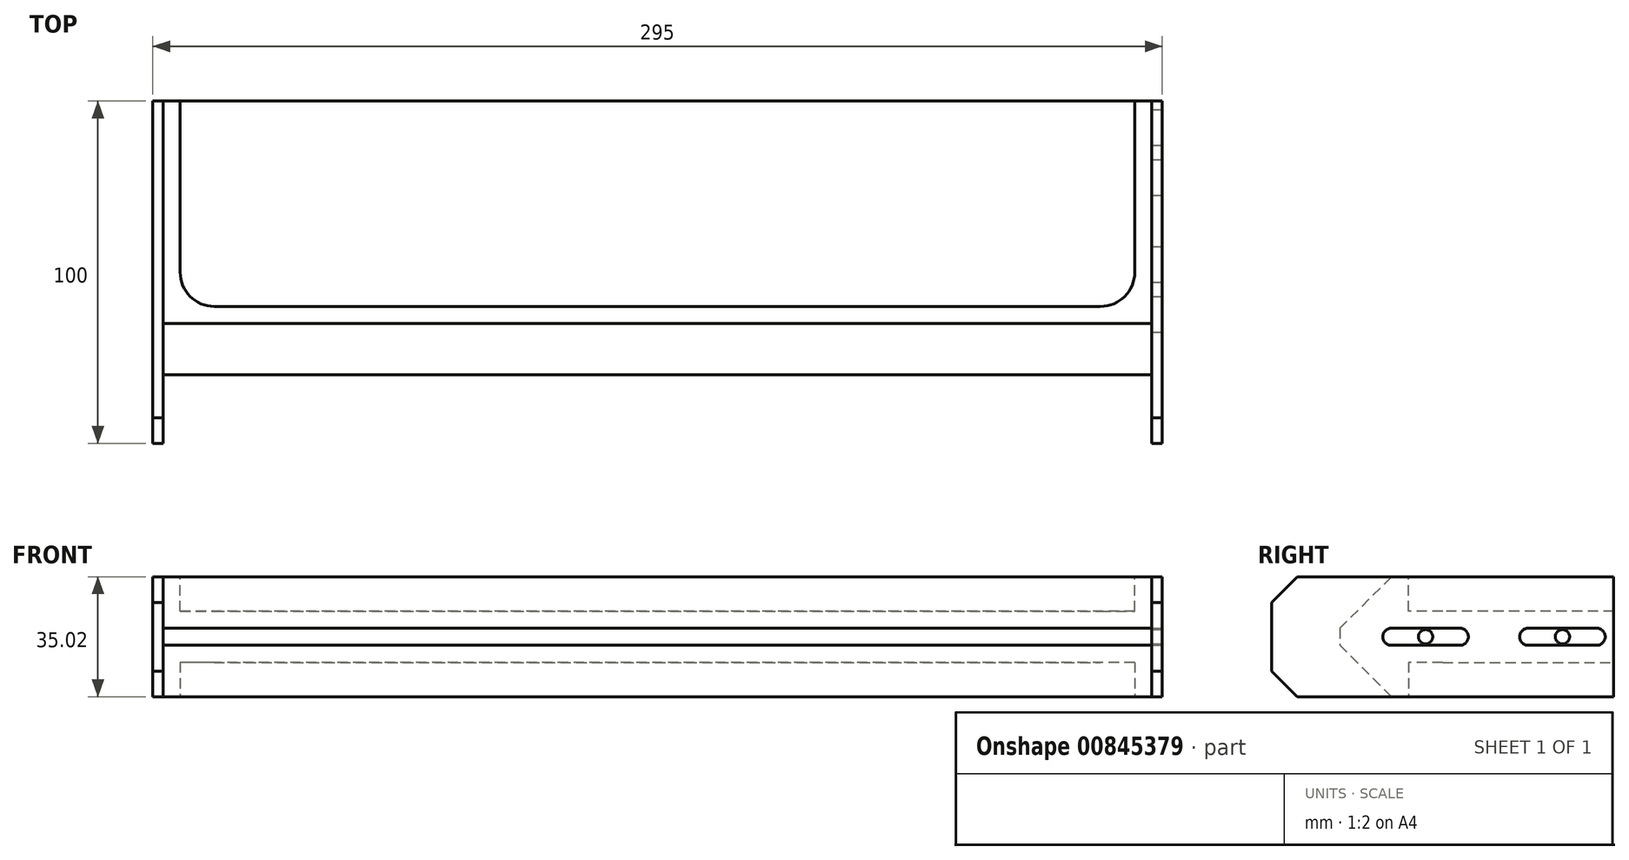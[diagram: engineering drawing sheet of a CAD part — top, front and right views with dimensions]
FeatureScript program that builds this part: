
annotation { "Feature Type Name" : "Feature", "Feature Type Description" : "" }
export const myFeature = defineFeature(function(context is Context, id is Id, definition is map)
    precondition{}
    {
        {
            var Q0;
            Q0=qCreatedBy(makeId("Top.planeOp"),FACE);
            var sketch = newSketch(context, id + "F0", { "sketchPlane" : qUnion([Q0])});
            skLineSegment(sketch, "E0.bottom", {"start": v(147.5, 50) * mm, "end": v(-147.5, 50) * mm});
            skLineSegment(sketch, "E0.top", {"start": v(147.5, -50) * mm, "end": v(144.5, -50) * mm});
            skLineSegment(sketch, "E0.left", {"start": v(147.5, 50) * mm, "end": v(147.5, -50) * mm});
            skLineSegment(sketch, "E0.right", {"start": v(-147.5, 50) * mm, "end": v(-147.5, -50) * mm});
            skPoint(sketch, "E0.middle", {"position": v(0, 0) * mm});
            skLineSegment(sketch, "E1", {"start": v(-144.5, -50) * mm, "end": v(-144.5, -30) * mm});
            skLineSegment(sketch, "E2", {"start": v(-144.5, -30) * mm, "end": v(144.5, -30) * mm});
            skLineSegment(sketch, "E3", {"start": v(144.5, -30) * mm, "end": v(144.5, -50) * mm});
            skLineSegment(sketch, "E4.trimOffspring", {"start": v(-144.5, -50) * mm, "end": v(-147.5, -50) * mm});
            skSolve(sketch);
        }
        {
            var Q0;
            Q0=qSketchRegion(id+"F0",true);
            extrude(context, id + "F1", {"entities" : qUnion([Q0]), "depth" : 17.5 * mm, "offsetDistance" : 25 * mm, "hasSecondDirection" : true, "secondDirectionOppositeDirection" : true, "secondDirectionDepth" : 17.5 * mm});
        }
        {
            var Q0;
            Q0=makeQuery(id+"F1.opExtrude","CAP_EDGE",EDGE,{"disambiguationData":[OSD([sQuery(id+"F0.wireOp",EDGE,"E2")])],"isStart":false});
            var Q1;
            Q1=makeQuery(id+"F1.opExtrude","CAP_EDGE",EDGE,{"disambiguationData":[OSD([sQuery(id+"F0.wireOp",EDGE,"E2")])],"isStart":true});
            chamfer(context, id + "F2", {"entities" : qUnion([Q0, Q1]), "width" : 15 * mm, "tangentPropagation" : true});
        }
        {
            var Q0;
            Q0=makeQuery(id+"F1.opExtrude","CAP_EDGE",EDGE,{"disambiguationData":[OSD([sQuery(id+"F0.wireOp",EDGE,"E0.top")])],"isStart":false});
            var Q1;
            Q1=makeQuery(id+"F1.opExtrude","CAP_EDGE",EDGE,{"disambiguationData":[OSD([sQuery(id+"F0.wireOp",EDGE,"E0.top")])],"isStart":true});
            var Q2;
            Q2=makeQuery(id+"F1.opExtrude","CAP_EDGE",EDGE,{"disambiguationData":[OSD([sQuery(id+"F0.wireOp",EDGE,"E4.trimOffspring")])],"isStart":false});
            var Q3;
            Q3=makeQuery(id+"F1.opExtrude","CAP_EDGE",EDGE,{"disambiguationData":[OSD([sQuery(id+"F0.wireOp",EDGE,"E4.trimOffspring")])],"isStart":true});
            chamfer(context, id + "F3", {"entities" : qUnion([Q0, Q1, Q2, Q3]), "width" : 7.5 * mm, "tangentPropagation" : true});
        }
        {
            var Q0;
            Q0=makeQuery(id+"F1.opExtrude","SWEPT_FACE",FACE,{"disambiguationData":[OSD([sQuery(id+"F0.wireOp",EDGE,"E0.left")])]});
            var sketch = newSketch(context, id + "F4", { "sketchPlane" : qUnion([Q0])});
            skLineSegment(sketch, "E5.bottom", {"start": v(45, 2.5) * mm, "end": v(25, 2.5) * mm});
            skLineSegment(sketch, "E5.top", {"start": v(45, -2.5) * mm, "end": v(25, -2.5) * mm});
            skLineSegment(sketch, "E5.left", {"start": v(47.5, 0) * mm, "end": v(47.5, 0) * mm});
            skLineSegment(sketch, "E5.right", {"start": v(22.5, 0) * mm, "end": v(22.5, 0) * mm});
            skLineSegment(sketch, "E6.bottom", {"start": v(5, 2.5) * mm, "end": v(-15, 2.5) * mm});
            skLineSegment(sketch, "E6.top", {"start": v(5, -2.5) * mm, "end": v(-15, -2.5) * mm});
            skLineSegment(sketch, "E6.left", {"start": v(7.5, 0) * mm, "end": v(7.5, 0) * mm});
            skLineSegment(sketch, "E6.right", {"start": v(-17.5, 0) * mm, "end": v(-17.5, 0) * mm});
            skPoint(sketch, "E7.visualSharp", {"position": v(-17.5, 2.5) * mm});
            skArc(sketch, "E7.filletArc", {"start": v(-15, 2.5) * mm, "mid": v(-16.77, 1.77) * mm, "end": v(-17.5, 0) * mm});
            skPoint(sketch, "E8.visualSharp", {"position": v(-17.5, -2.5) * mm});
            skArc(sketch, "E8.filletArc", {"start": v(-17.5, 0) * mm, "mid": v(-16.77, -1.77) * mm, "end": v(-15, -2.5) * mm});
            skPoint(sketch, "E9.visualSharp", {"position": v(7.5, 2.5) * mm});
            skArc(sketch, "E9.filletArc", {"start": v(7.5, 0) * mm, "mid": v(6.77, 1.77) * mm, "end": v(5, 2.5) * mm});
            skPoint(sketch, "E10.visualSharp", {"position": v(7.5, -2.5) * mm});
            skArc(sketch, "E10.filletArc", {"start": v(5, -2.5) * mm, "mid": v(6.77, -1.77) * mm, "end": v(7.5, 0) * mm});
            skPoint(sketch, "E11.visualSharp", {"position": v(22.5, 2.5) * mm});
            skArc(sketch, "E11.filletArc", {"start": v(25, 2.5) * mm, "mid": v(23.23, 1.77) * mm, "end": v(22.5, 0) * mm});
            skPoint(sketch, "E12.visualSharp", {"position": v(22.5, -2.5) * mm});
            skArc(sketch, "E12.filletArc", {"start": v(22.5, 0) * mm, "mid": v(23.23, -1.77) * mm, "end": v(25, -2.5) * mm});
            skPoint(sketch, "E13.visualSharp", {"position": v(47.5, 2.5) * mm});
            skArc(sketch, "E13.filletArc", {"start": v(47.5, 0) * mm, "mid": v(46.77, 1.77) * mm, "end": v(45, 2.5) * mm});
            skPoint(sketch, "E14.visualSharp", {"position": v(47.5, -2.5) * mm});
            skArc(sketch, "E14.filletArc", {"start": v(45, -2.5) * mm, "mid": v(46.77, -1.77) * mm, "end": v(47.5, 0) * mm});
            skCircle(sketch, "E15", {"center": v(-5, 0) * mm, "radius": 2.1 * mm});
            skCircle(sketch, "E16", {"center": v(35, 0) * mm, "radius": 2.1 * mm});
            skPoint(sketch, "E16.centerSnap0", {"position": v(35, -2.5) * mm});
            skLineSegment(sketch, "E17", {"start": v(-50, 0) * mm, "end": v(50, 0) * mm, "construction": true});
            skSolve(sketch);
        }
        {
            var Q0;
            Q0=makeQuery(id+"F1.opExtrude","CAP_FACE",FACE,{"disambiguationData":[OSD([sQuery(id+"F0.wireOp",EDGE,"E0.bottom"),sQuery(id+"F0.wireOp",EDGE,"E0.top"),sQuery(id+"F0.wireOp",EDGE,"E0.left"),sQuery(id+"F0.wireOp",EDGE,"E0.right"),sQuery(id+"F0.wireOp",EDGE,"E1"),sQuery(id+"F0.wireOp",EDGE,"E2"),sQuery(id+"F0.wireOp",EDGE,"E3"),sQuery(id+"F0.wireOp",EDGE,"E4.trimOffspring")])],"isStart":false});
            var sketch = newSketch(context, id + "F5", { "sketchPlane" : qUnion([Q0])});
            skLineSegment(sketch, "E18.bottom", {"start": v(-147.5, 50) * mm, "end": v(-144.5, 50) * mm});
            skLineSegment(sketch, "E18.top", {"start": v(-147.5, -42.5) * mm, "end": v(-144.5, -42.5) * mm});
            skLineSegment(sketch, "E18.left", {"start": v(-147.5, 50) * mm, "end": v(-147.5, -42.5) * mm});
            skLineSegment(sketch, "E18.right", {"start": v(-144.5, 50) * mm, "end": v(-144.5, -42.5) * mm});
            skLineSegment(sketch, "E19.bottom", {"start": v(147.5, 50) * mm, "end": v(144.5, 50) * mm});
            skLineSegment(sketch, "E19.top", {"start": v(147.5, -42.5) * mm, "end": v(144.5, -42.5) * mm});
            skLineSegment(sketch, "E19.left", {"start": v(147.5, 50) * mm, "end": v(147.5, -42.5) * mm});
            skLineSegment(sketch, "E19.right", {"start": v(144.5, 50) * mm, "end": v(144.5, -42.5) * mm});
            skSolve(sketch);
        }
        {
            var Q0;
            Q0 = qSketchRegion(id + "F5", true);
            extrude(context, id + "F6", {"entities" : qUnion([Q0]), "operationType" : NewBodyOperationType.ADD, "depth" : 0.01 * mm, "offsetDistance" : 25 * mm});
        }
        {
            var Q0;
            Q0=makeQuery(id+"F1.opExtrude","CAP_FACE",FACE,{"disambiguationData":[OSD([sQuery(id+"F0.wireOp",EDGE,"E0.bottom"),sQuery(id+"F0.wireOp",EDGE,"E0.top"),sQuery(id+"F0.wireOp",EDGE,"E0.left"),sQuery(id+"F0.wireOp",EDGE,"E0.right"),sQuery(id+"F0.wireOp",EDGE,"E1"),sQuery(id+"F0.wireOp",EDGE,"E2"),sQuery(id+"F0.wireOp",EDGE,"E3"),sQuery(id+"F0.wireOp",EDGE,"E4.trimOffspring")])],"isStart":true});
            var sketch = newSketch(context, id + "F7", { "sketchPlane" : qUnion([Q0])});
            skLineSegment(sketch, "E20.bottom", {"start": v(-147.5, -50) * mm, "end": v(-144.5, -50) * mm});
            skLineSegment(sketch, "E20.top", {"start": v(-147.5, 42.5) * mm, "end": v(-144.5, 42.5) * mm});
            skLineSegment(sketch, "E20.left", {"start": v(-147.5, -50) * mm, "end": v(-147.5, 42.5) * mm});
            skLineSegment(sketch, "E20.right", {"start": v(-144.5, -50) * mm, "end": v(-144.5, 42.5) * mm});
            skLineSegment(sketch, "E21.bottom", {"start": v(147.5, -50) * mm, "end": v(144.5, -50) * mm});
            skLineSegment(sketch, "E21.top", {"start": v(147.5, 42.5) * mm, "end": v(144.5, 42.5) * mm});
            skLineSegment(sketch, "E21.left", {"start": v(147.5, -50) * mm, "end": v(147.5, 42.5) * mm});
            skLineSegment(sketch, "E21.right", {"start": v(144.5, -50) * mm, "end": v(144.5, 42.5) * mm});
            skSolve(sketch);
        }
        {
            var Q0;
            Q0 = qSketchRegion(id + "F7", true);
            extrude(context, id + "F8", {"entities" : qUnion([Q0]), "operationType" : NewBodyOperationType.ADD, "depth" : 0.01 * mm, "offsetDistance" : 25 * mm});
        }
        {
            var Q0;
            Q0=makeQuery(id+"F4.imprint","IMPRINT",FACE,{"disambiguationData":[TD([[makeQuery(id+"F4.imprint","IMPRINT",EDGE,{"derivedFrom":sQuery(id+"F4.wireOp",EDGE,"E5.bottom")}),1.0]])]});
            var Q1;
            Q1=makeQuery(id+"F4.imprint","IMPRINT",FACE,{"disambiguationData":[TD([[makeQuery(id+"F4.imprint","IMPRINT",EDGE,{"derivedFrom":sQuery(id+"F4.wireOp",EDGE,"E6.bottom")}),1.0]])]});
            extrude(context, id + "F9", {"entities" : qUnion([Q0, Q1]), "operationType" : NewBodyOperationType.REMOVE, "oppositeDirection" : true, "depth" : 3 * mm, "offsetDistance" : 25 * mm});
        }
        {
            var Q0;
            Q0=makeQuery(id+"F1.opExtrude","CAP_FACE",FACE,{"disambiguationData":[OSD([sQuery(id+"F0.wireOp",EDGE,"E0.bottom"),sQuery(id+"F0.wireOp",EDGE,"E0.top"),sQuery(id+"F0.wireOp",EDGE,"E0.left"),sQuery(id+"F0.wireOp",EDGE,"E0.right"),sQuery(id+"F0.wireOp",EDGE,"E1"),sQuery(id+"F0.wireOp",EDGE,"E2"),sQuery(id+"F0.wireOp",EDGE,"E3"),sQuery(id+"F0.wireOp",EDGE,"E4.trimOffspring")])],"isStart":false});
            var sketch = newSketch(context, id + "F10", { "sketchPlane" : qUnion([Q0])});
            skLineSegment(sketch, "E22.bottom", {"start": v(-139.5, 50) * mm, "end": v(139.5, 50) * mm});
            skLineSegment(sketch, "E22.top", {"start": v(-129.5, -10) * mm, "end": v(129.5, -10) * mm});
            skLineSegment(sketch, "E22.left", {"start": v(-139.5, 50) * mm, "end": v(-139.5, 0) * mm});
            skLineSegment(sketch, "E22.right", {"start": v(139.5, 50) * mm, "end": v(139.5, 0) * mm});
            skPoint(sketch, "E23.visualSharp", {"position": v(-139.5, -10) * mm});
            skArc(sketch, "E23.filletArc", {"start": v(-139.5, 0) * mm, "mid": v(-136.57, -7.07) * mm, "end": v(-129.5, -10) * mm});
            skPoint(sketch, "E24.visualSharp", {"position": v(139.5, -10) * mm});
            skArc(sketch, "E24.filletArc", {"start": v(129.5, -10) * mm, "mid": v(136.57, -7.07) * mm, "end": v(139.5, 0) * mm});
            skSolve(sketch);
        }
        {
            var Q0;
            Q0=makeQuery(id+"F10.imprint","IMPRINT",FACE,{"disambiguationData":[TD([[makeQuery(id+"F10.imprint","IMPRINT",EDGE,{"derivedFrom":sQuery(id+"F10.wireOp",EDGE,"E22.bottom")}),1.0]])]});
            extrude(context, id + "F11", {"entities" : qUnion([Q0]), "operationType" : NewBodyOperationType.REMOVE, "oppositeDirection" : true, "depth" : 10 * mm, "offsetDistance" : 25 * mm});
        }
        {
            var Q0;
            Q0=makeQuery(id+"F1.opExtrude","CAP_FACE",FACE,{"disambiguationData":[OSD([sQuery(id+"F0.wireOp",EDGE,"E0.bottom"),sQuery(id+"F0.wireOp",EDGE,"E0.top"),sQuery(id+"F0.wireOp",EDGE,"E0.left"),sQuery(id+"F0.wireOp",EDGE,"E0.right"),sQuery(id+"F0.wireOp",EDGE,"E1"),sQuery(id+"F0.wireOp",EDGE,"E2"),sQuery(id+"F0.wireOp",EDGE,"E3"),sQuery(id+"F0.wireOp",EDGE,"E4.trimOffspring")])],"isStart":true});
            var sketch = newSketch(context, id + "F12", { "sketchPlane" : qUnion([Q0])});
            skLineSegment(sketch, "E25.0.0", {"start": v(139.5, 0) * mm, "end": v(139.5, -50) * mm});
            skLineSegment(sketch, "E25.0.1", {"start": v(139.5, -50) * mm, "end": v(-139.5, -50) * mm});
            skLineSegment(sketch, "E25.0.2", {"start": v(-139.5, -50) * mm, "end": v(-139.5, 0) * mm});
            skArc(sketch, "E25.0.3", {"start": v(-139.5, 0) * mm, "mid": v(-136.57, 7.07) * mm, "end": v(-129.5, 10) * mm});
            skLineSegment(sketch, "E25.0.4", {"start": v(-129.5, 10) * mm, "end": v(129.5, 10) * mm});
            skArc(sketch, "E25.0.5", {"start": v(129.5, 10) * mm, "mid": v(136.57, 7.07) * mm, "end": v(139.5, 0) * mm});
            skSolve(sketch);
        }
        {
            var Q0;
            Q0 = qSketchRegion(id + "F12", true);
            extrude(context, id + "F13", {"entities" : qUnion([Q0]), "operationType" : NewBodyOperationType.REMOVE, "oppositeDirection" : true, "depth" : 10 * mm, "offsetDistance" : 25 * mm});
        }
    });
